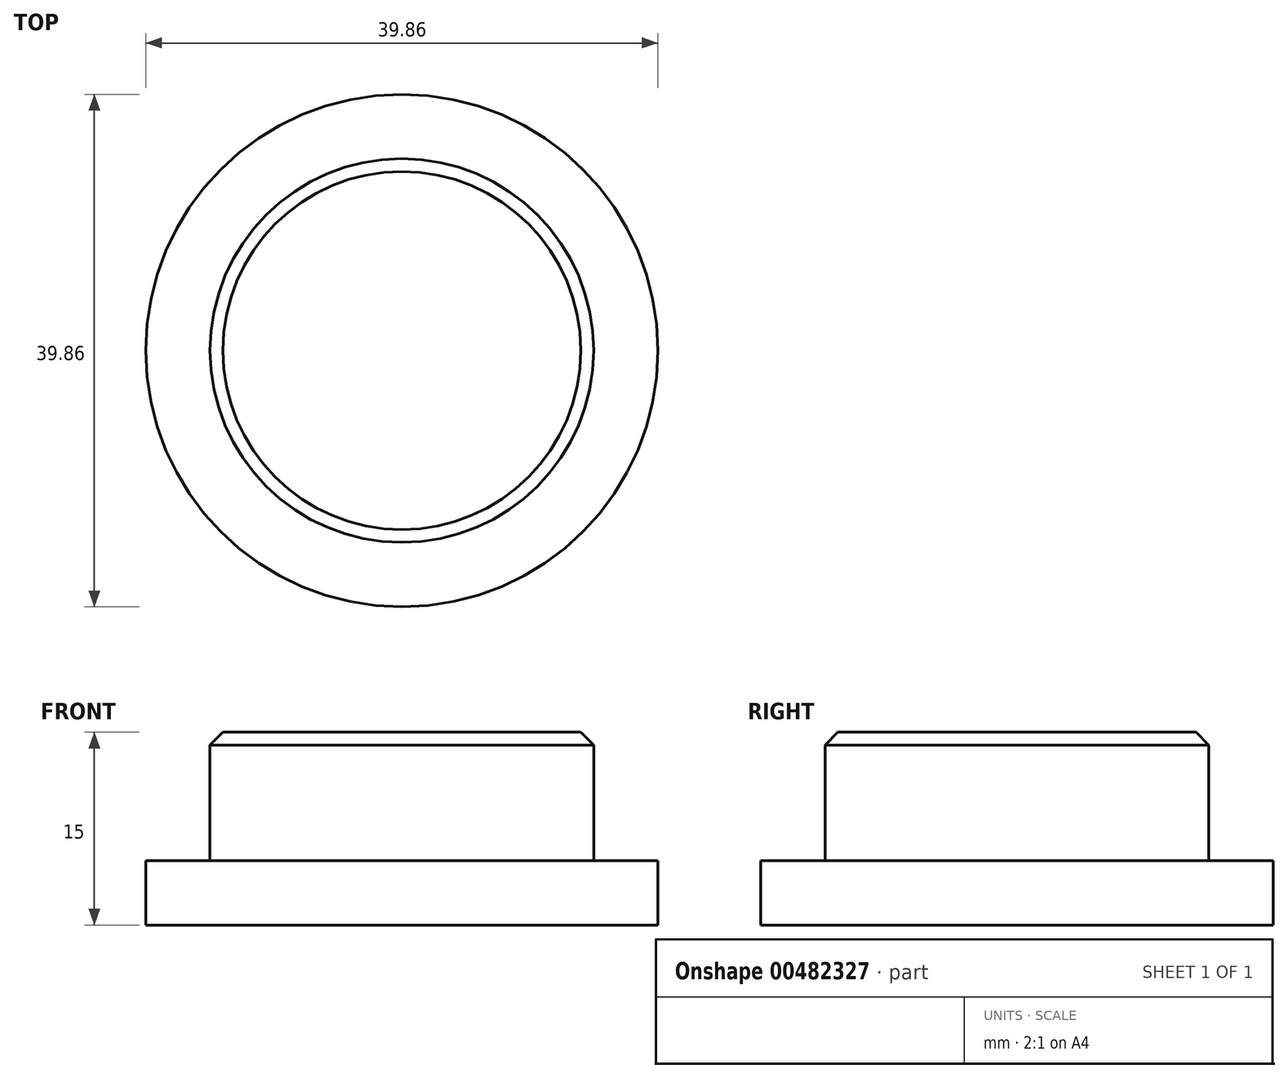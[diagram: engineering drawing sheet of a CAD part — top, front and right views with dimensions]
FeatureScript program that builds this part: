
annotation { "Feature Type Name" : "Feature", "Feature Type Description" : "" }
export const myFeature = defineFeature(function(context is Context, id is Id, definition is map)
    precondition{}
    {
        {
            var Q0;
            Q0=qCreatedBy(makeId("Top.planeOp"),FACE);
            var sketch = newSketch(context, id + "F0", { "sketchPlane" : qUnion([Q0])});
            skCircle(sketch, "E0", {"center": v(0, 0) * mm, "radius": 14.93 * mm});
            skCircle(sketch, "E1.0", {"center": v(0, 0) * mm, "radius": 19.93 * mm});
            skSolve(sketch);
        }
        {
            var Q0;
            Q0 = qSketchRegion(id + "F0", true);
            var Q1;
            Q1=makeQuery(id+"F0.imprint","IMPRINT",FACE,{"disambiguationData":[TD([[makeQuery(id+"F0.imprint","IMPRINT",EDGE,{"derivedFrom":sQuery(id+"F0.wireOp",EDGE,"E0")}),1.0]])]});
            extrude(context, id + "F1", {"entities" : qUnion([Q0, Q1]), "depth" : 5 * mm});
        }
        {
            var Q0;
            Q0=makeQuery(id+"F0.imprint","IMPRINT",FACE,{"disambiguationData":[TD([[makeQuery(id+"F0.imprint","IMPRINT",EDGE,{"derivedFrom":sQuery(id+"F0.wireOp",EDGE,"E0")}),1.0]])]});
            extrude(context, id + "F2", {"entities" : qUnion([Q0]), "operationType" : NewBodyOperationType.ADD, "depth" : 15 * mm});
        }
        {
            var Q0;
            Q0=makeQuery(id+"F2.opExtrude","CAP_EDGE",EDGE,{"disambiguationData":[OSD([sQuery(id+"F0.wireOp",EDGE,"E0")])],"isStart":false});
            chamfer(context, id + "F3", {"entities" : qUnion([Q0]), "width" : 1 * mm, "tangentPropagation" : true});
        }
    });
